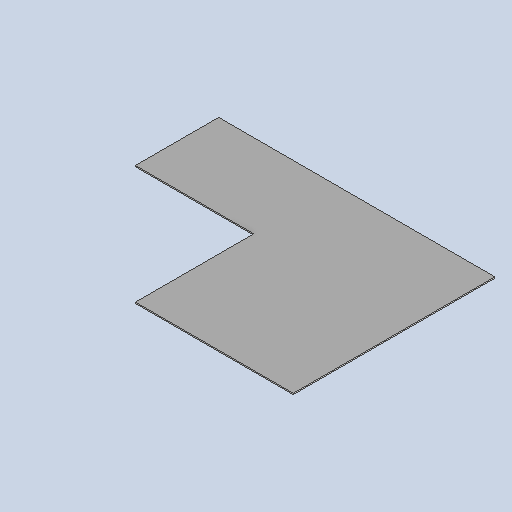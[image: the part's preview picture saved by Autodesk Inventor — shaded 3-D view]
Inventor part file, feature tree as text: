
AUTODESK INVENTOR PART (.ipt)
format: ipt  version: 2025 (Build 290162010, 162A)  size: 115,712 bytes
history: native  units: mm
features: other x3, sketch x2, sheet_metal_op x1, extrude x1
ambient origin geometry x8: Origin, YZ Plane, XZ Plane, XY Plane, X Axis, Y Axis, Z Axis, Center Point
bodies: Solid1 (feature_tree)
feature tree (7):
  other  "BSH 035 board cone 5"
  sheet_metal_op  "Face1"
  extrude  "Extrusion2"  Depth=511.0mm
  sketch  "Sketch1"  dims[d0=700.0mm d1=511.0mm]
  other  "Plate1"
  sketch  "Sketch6"  dims[d2=3.0mm d36=300.0mm d37=300.0mm d38=10.0mm d39=0.0mm]
  other  "Definition1"
